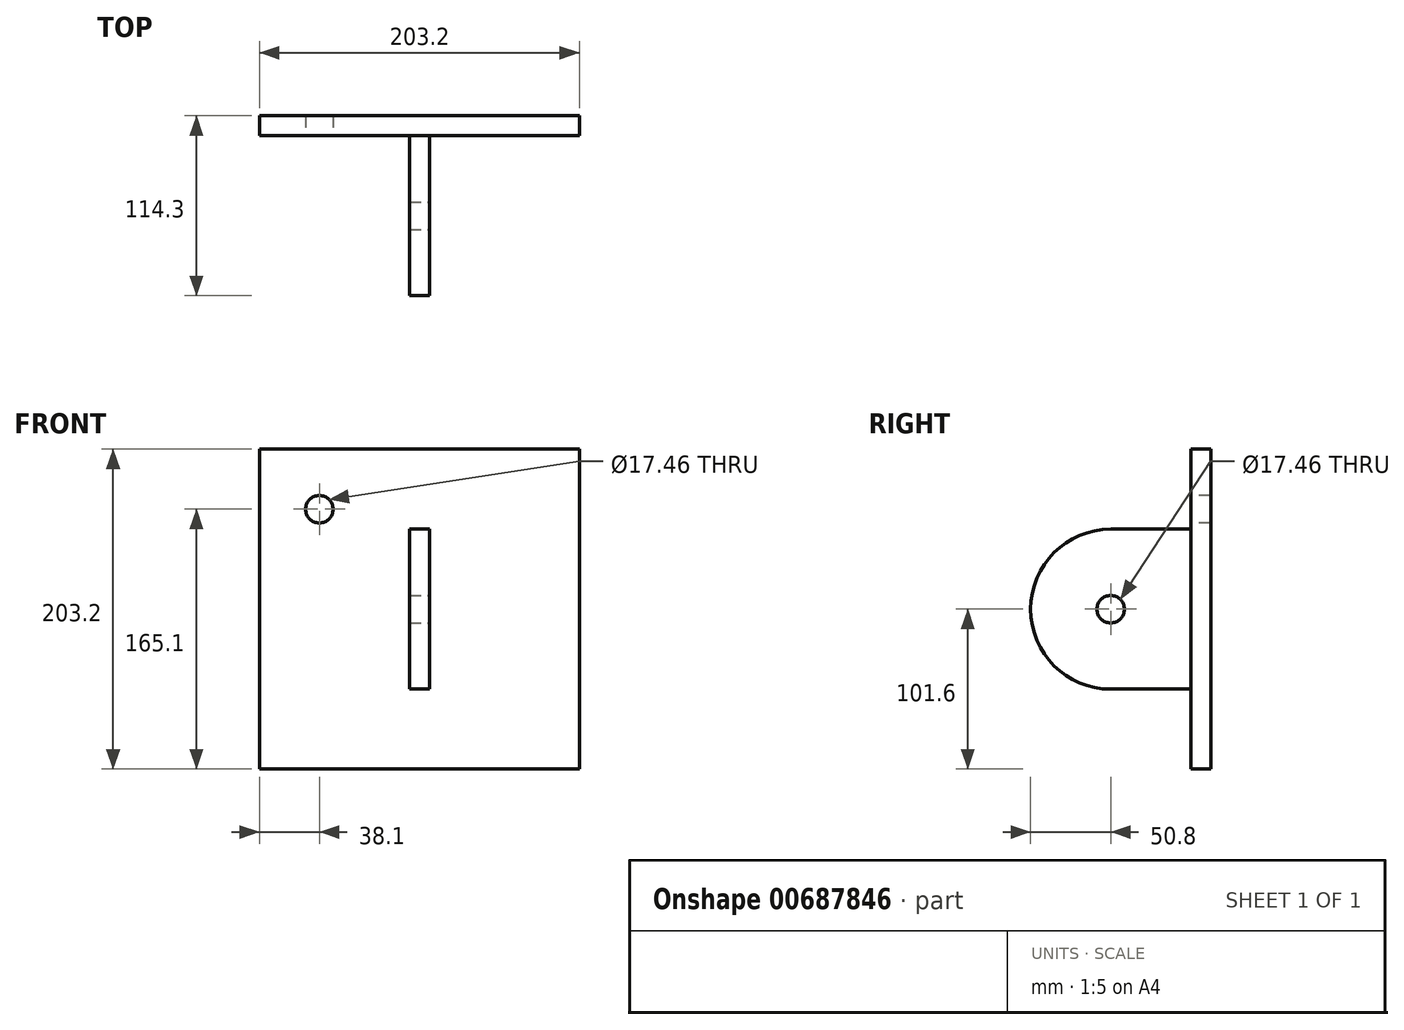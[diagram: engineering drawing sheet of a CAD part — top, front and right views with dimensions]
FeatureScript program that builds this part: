
annotation { "Feature Type Name" : "Feature", "Feature Type Description" : "" }
export const myFeature = defineFeature(function(context is Context, id is Id, definition is map)
    precondition{}
    {
        {
            var Q0;
            Q0=qCreatedBy(makeId("Front.planeOp"),FACE);
            var sketch = newSketch(context, id + "F0", { "sketchPlane" : qUnion([Q0])});
            skLineSegment(sketch, "E0.bottom", {"start": v(101.6, 101.6) * mm, "end": v(-101.6, 101.6) * mm});
            skLineSegment(sketch, "E0.top", {"start": v(101.6, -101.6) * mm, "end": v(-101.6, -101.6) * mm});
            skLineSegment(sketch, "E0.left", {"start": v(101.6, 101.6) * mm, "end": v(101.6, -101.6) * mm});
            skLineSegment(sketch, "E0.right", {"start": v(-101.6, 101.6) * mm, "end": v(-101.6, -101.6) * mm});
            skPoint(sketch, "E0.middle", {"position": v(0, 0) * mm});
            skSolve(sketch);
        }
        {
            var Q0;
            Q0=makeQuery(id+"F0.imprint","IMPRINT",FACE,{"disambiguationData":[TD([[makeQuery(id+"F0.imprint","IMPRINT",EDGE,{"derivedFrom":sQuery(id+"F0.wireOp",EDGE,"E0.bottom")}),1.0]])]});
            extrude(context, id + "F1", {"entities" : qUnion([Q0]), "depth" : 12.7 * mm, "offsetDistance" : 25.4 * mm});
        }
        {
            var Q0;
            Q0=makeQuery(id+"F1.opExtrude","CAP_FACE",FACE,{"disambiguationData":[OSD([sQuery(id+"F0.wireOp",EDGE,"E0.bottom"),sQuery(id+"F0.wireOp",EDGE,"E0.top"),sQuery(id+"F0.wireOp",EDGE,"E0.left"),sQuery(id+"F0.wireOp",EDGE,"E0.right")])],"isStart":false});
            var sketch = newSketch(context, id + "F2", { "sketchPlane" : qUnion([Q0])});
            skLineSegment(sketch, "E1.bottom", {"start": v(6.35, 50.8) * mm, "end": v(-6.35, 50.8) * mm});
            skLineSegment(sketch, "E1.top", {"start": v(6.35, -50.8) * mm, "end": v(-6.35, -50.8) * mm});
            skLineSegment(sketch, "E1.left", {"start": v(6.35, 50.8) * mm, "end": v(6.35, -50.8) * mm});
            skLineSegment(sketch, "E1.right", {"start": v(-6.35, 50.8) * mm, "end": v(-6.35, -50.8) * mm});
            skPoint(sketch, "E1.middle", {"position": v(0, 0) * mm});
            skSolve(sketch);
        }
        {
            var Q0;
            Q0=makeQuery(id+"F2.imprint","IMPRINT",FACE,{"disambiguationData":[TD([[makeQuery(id+"F2.imprint","IMPRINT",EDGE,{"derivedFrom":sQuery(id+"F2.wireOp",EDGE,"E1.bottom")}),1.0]])]});
            extrude(context, id + "F3", {"entities" : qUnion([Q0]), "operationType" : NewBodyOperationType.ADD, "depth" : 101.6 * mm, "offsetDistance" : 25.4 * mm});
        }
        {
            var Q0;
            Q0=makeQuery(id+"F3.opExtrude","CAP_EDGE",EDGE,{"disambiguationData":[OSD([sQuery(id+"F2.wireOp",EDGE,"E1.bottom")])],"isStart":false});
            var Q1;
            Q1=makeQuery(id+"F3.opExtrude","CAP_EDGE",EDGE,{"disambiguationData":[OSD([sQuery(id+"F2.wireOp",EDGE,"E1.top")])],"isStart":false});
            fillet(context, id + "F4", {"entities" : qUnion([Q0, Q1]), "radius" : 50.8 * mm, "tangentPropagation" : true, "allowEdgeOverflow" : false});
        }
        {
            var Q0;
            Q0=makeQuery(id+"F3.opExtrude","SWEPT_FACE",FACE,{"disambiguationData":[OSD([sQuery(id+"F2.wireOp",EDGE,"E1.left")])]});
            var sketch = newSketch(context, id + "F5", { "sketchPlane" : qUnion([Q0])});
            skCircle(sketch, "E2", {"center": v(-63.5, 0) * mm, "radius": 8.73 * mm});
            skSolve(sketch);
        }
        {
            var Q0;
            Q0=makeQuery(id+"F5.imprint","IMPRINT",FACE,{"disambiguationData":[TD([[makeQuery(id+"F5.imprint","IMPRINT",EDGE,{"derivedFrom":sQuery(id+"F5.wireOp",EDGE,"E2")}),1.0]])]});
            extrude(context, id + "F6", {"entities" : qUnion([Q0]), "operationType" : NewBodyOperationType.REMOVE, "oppositeDirection" : true, "depth" : 25.4 * mm, "offsetDistance" : 25.4 * mm});
        }
        {
            var Q0;
            Q0=makeQuery(id+"F1.opExtrude","CAP_FACE",FACE,{"disambiguationData":[OSD([sQuery(id+"F0.wireOp",EDGE,"E0.bottom"),sQuery(id+"F0.wireOp",EDGE,"E0.top"),sQuery(id+"F0.wireOp",EDGE,"E0.left"),sQuery(id+"F0.wireOp",EDGE,"E0.right")])],"isStart":false});
            var sketch = newSketch(context, id + "F7", { "sketchPlane" : qUnion([Q0])});
            skCircle(sketch, "E3", {"center": v(-63.5, 63.5) * mm, "radius": 8.73 * mm});
            skSolve(sketch);
        }
        {
            var Q0;
            Q0=makeQuery(id+"F7.imprint","IMPRINT",FACE,{"disambiguationData":[TD([[makeQuery(id+"F7.imprint","IMPRINT",EDGE,{"derivedFrom":sQuery(id+"F7.wireOp",EDGE,"E3")}),1.0]])]});
            extrude(context, id + "F8", {"entities" : qUnion([Q0]), "operationType" : NewBodyOperationType.REMOVE, "oppositeDirection" : true, "depth" : 25.4 * mm, "offsetDistance" : 25.4 * mm});
        }
        {
            var Q0;
            Q0=qCreatedBy(makeId("Right.planeOp"),FACE);
            var sketch = newSketch(context, id + "F9", { "sketchPlane" : qUnion([Q0])});
            skLineSegment(sketch, "E4", {"start": v(0, 0) * mm, "end": v(-139.1, 0) * mm, "construction": true});
            skSolve(sketch);
        }
    });
